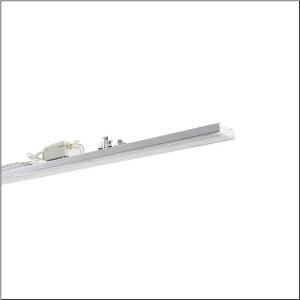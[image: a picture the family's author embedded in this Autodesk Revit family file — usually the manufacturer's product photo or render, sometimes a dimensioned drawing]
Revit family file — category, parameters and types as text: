
# Revit family: licross_21_recessed_mo_52tl107n485g
name_source: partatom
category: Lighting Fixtures
units: mm (PartAtom-declared; Revit-internal decimal feet)

## family parameters
Cut with Voids When Loaded = No
Host = Face
Light Source = No
Part Type = Normal
Room Calculation Point = No
Round Connector Dimension = Use Diameter
Shared = No

## types (1)
- Licross 21 Recessed MO (1 x LED, 8580 lm, 47.9 W, 4000K)
    Apparent Load = 48 VA
    CIE Flux Codes = 50 81 96 100 100
    Color Rendering = 80
    Color Temperature = 4000K
    Default Elevation = 1800 mm
    Description = Licross 21 Recessed MO, luminaire insert, of sheet steel, galvanised, coil coated, white, length: 1.500mm, width: 66mm, height: 67mm, LED rated luminous flux: 8.560lm, light colour: 840, SDCM (Standard Deviation of Colour Matching)MacAdam ≤ 3 SDCM (initial), control gear: ON/OFF, with plug, 3-pole, with phase selection, mains connection: 220..240V, AC, 50/60Hz, rated input power: 48W, internal wiring halogen-free, primary optical cover: cover, of PMMA, light emission: direct distribution, primary light characteristic: symmetric, protection rating (complete): IP40, insulation class (complete): insulation class I (protective earthing), certification: CE, ENEC, VDE, UKCA, protection symbol: D if used in an environment without relevant dust loads with corresponding accessories, impact resistance: IK06, permissible ambient temperature for indoor applications: -35..+40°C, corresponds to IFS (International Featured Standards) requirements for safety and quality in the food industry, reducing of maximum allowable ambient temperature of 5°C with ceiling mounting, LABS conformity tested according to VDMA 24364:2018-05, The light source and the operating device comply with the requirements of the Ecodesign Regulation (EU) 2019/2020 and are replaceable in accordance with this regulation, packaging unit: 1 piece
    Height = 58 mm
    Lamp = 1 x LED
    Lamp Light Flux = 8580 lm
    Lamp Power = 47.9 W
    Lamp count = 1
    Length = 1500 mm
    Luminous efficacy = 179 lm/W
    Manufacturer = Siteco
    ModVariant = No
    Model = 52TL107N485G
    Mounting Place = Ceiling
    Mounting Type = Pendant
    Number of Poles = 1
    OnlyDefault = Yes
    Power Factor = 1
    Product Name = Licross 21 Recessed MO
    Product group = luminaire insert | ceiling pendant
    ProductGroupID = 901
    Protection Class = Protection class I
    Protection Degree = IP 40
    RLX_Detail_Level = 1
    RLX_Emergency_Light_Flux = 0 lm
    RLX_Emergency_Type = 0
    RLX_Emergency_Type_DB = No
    RlxData = <blob elided: 21013 chars, md5=1d365803>
    Socket = socket
    Standby Power = 0 W
    System Light Flux = 8580 lm
    System Power = 48 W
    Type Comments = Product without accessories
    Type Image = l_1296930.jpg
    URL = http://relux.com
    VarID = ---
    Voltage = 0 V
    Weight = 0.00 kg
    Width = 66 mm

## geometry (parser evidence)
native form markers: Blend x4, Sweep x11
no freeform markers — native parametric forms only
